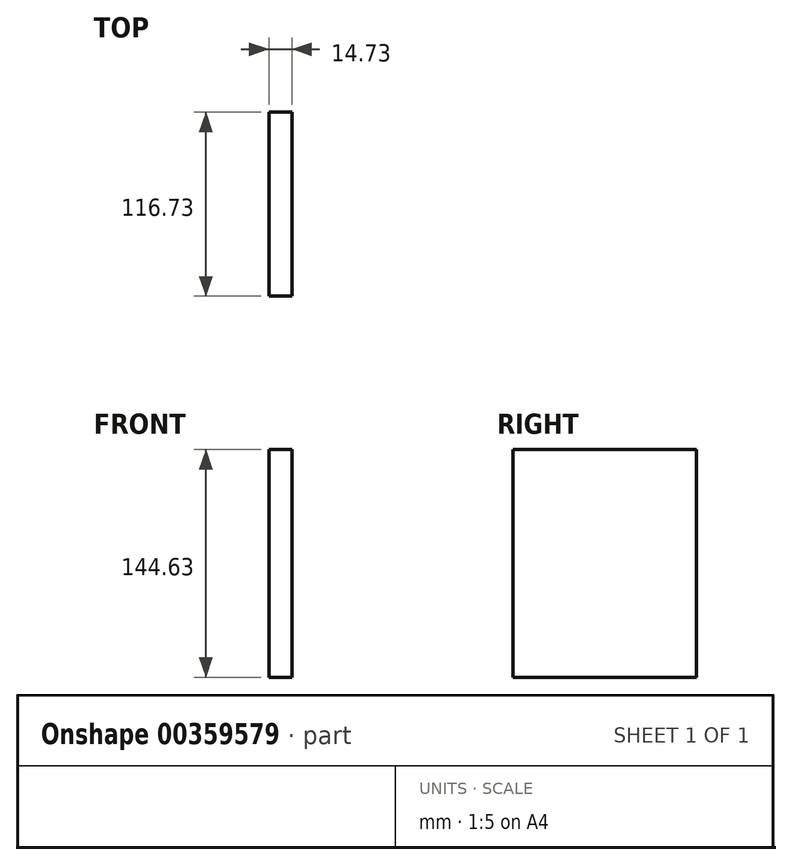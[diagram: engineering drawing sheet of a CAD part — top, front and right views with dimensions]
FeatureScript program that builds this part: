
annotation { "Feature Type Name" : "Feature", "Feature Type Description" : "" }
export const myFeature = defineFeature(function(context is Context, id is Id, definition is map)
    precondition{}
    {
        {
            var Q0;
            Q0=qCreatedBy(makeId("Right.planeOp"),FACE);
            var sketch = newSketch(context, id + "F0", { "sketchPlane" : qUnion([Q0])});
            skLineSegment(sketch, "E0.bottom", {"start": v(-43.22, 67.42) * mm, "end": v(73.5, 67.42) * mm});
            skLineSegment(sketch, "E0.top", {"start": v(-43.22, -77.21) * mm, "end": v(73.5, -77.21) * mm});
            skLineSegment(sketch, "E0.left", {"start": v(-43.22, 67.42) * mm, "end": v(-43.22, -77.21) * mm});
            skLineSegment(sketch, "E0.right", {"start": v(73.5, 67.42) * mm, "end": v(73.5, -77.21) * mm});
            skSolve(sketch);
        }
        {
            var Q0;
            Q0 = qSketchRegion(id + "F0", true);
            extrude(context, id + "F1", {"entities" : qUnion([Q0]), "depth" : 14.73 * mm});
        }
    });
